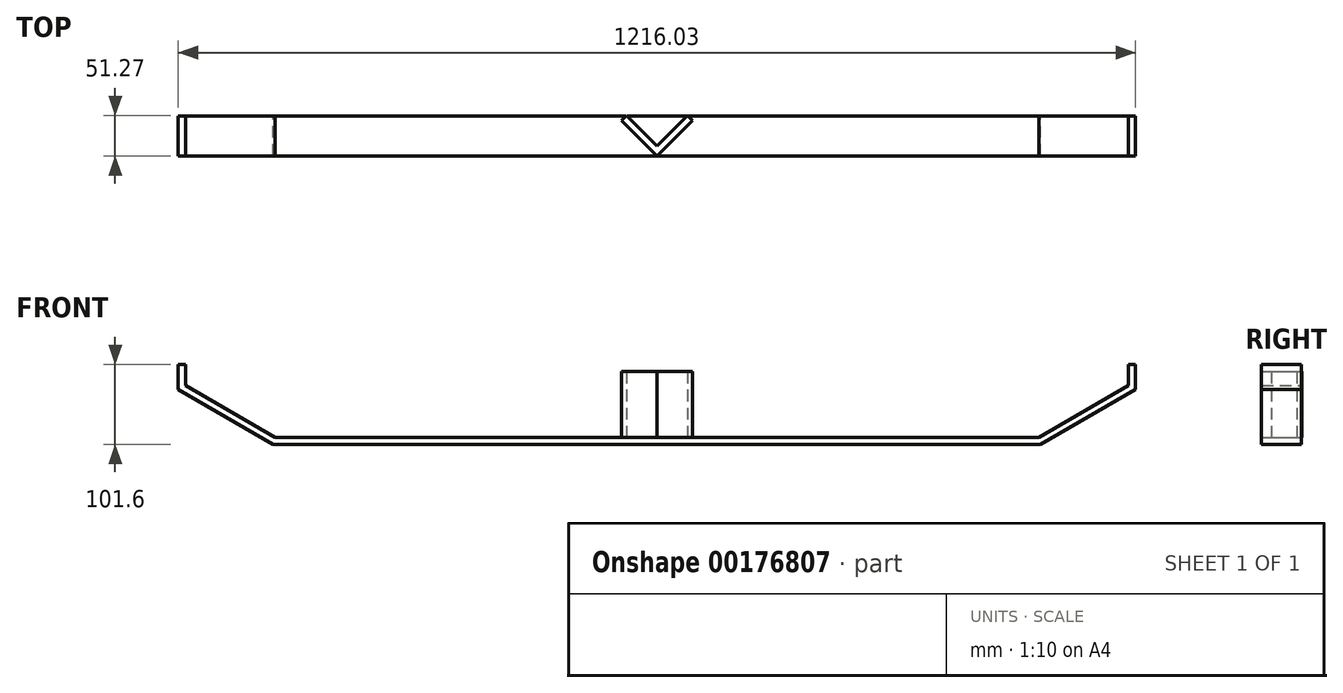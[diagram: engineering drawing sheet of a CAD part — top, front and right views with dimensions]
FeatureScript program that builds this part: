
annotation { "Feature Type Name" : "Feature", "Feature Type Description" : "" }
export const myFeature = defineFeature(function(context is Context, id is Id, definition is map)
    precondition{}
    {
        {
            var Q0;
            Q0=qCreatedBy(makeId("Front.planeOp"),FACE);
            var sketch = newSketch(context, id + "F0", { "sketchPlane" : qUnion([Q0])});
            skLineSegment(sketch, "E0", {"start": v(0, 0) * mm, "end": v(974.73, 0) * mm});
            skLineSegment(sketch, "E1.0", {"start": v(1095.38, 69.66) * mm, "end": v(1095.38, 101.6) * mm});
            skLineSegment(sketch, "E2", {"start": v(974.73, 0) * mm, "end": v(1095.38, 69.66) * mm});
            skLineSegment(sketch, "E3", {"start": v(487.36, 0) * mm, "end": v(487.36, 114.97) * mm});
            skLineSegment(sketch, "E4.MirrorCS", {"start": v(0, 0) * mm, "end": v(-120.65, 69.66) * mm});
            skLineSegment(sketch, "E5.MirrorCS", {"start": v(-120.65, 69.66) * mm, "end": v(-120.65, 101.6) * mm});
            skLineSegment(sketch, "E6.0", {"start": v(-111.65, 74.85) * mm, "end": v(-111.65, 101.6) * mm});
            skLineSegment(sketch, "E7.0", {"start": v(2.41, 9) * mm, "end": v(-111.65, 74.85) * mm});
            skLineSegment(sketch, "E8.0", {"start": v(2.41, 9) * mm, "end": v(972.31, 9) * mm});
            skLineSegment(sketch, "E9.0", {"start": v(972.31, 9) * mm, "end": v(1086.38, 74.85) * mm});
            skLineSegment(sketch, "E10.0", {"start": v(1086.38, 74.85) * mm, "end": v(1086.38, 101.6) * mm});
            skLineSegment(sketch, "E11.filletArc", {"start": v(1086.38, 74.85) * mm, "end": v(1086.38, 74.85) * mm});
            skLineSegment(sketch, "E12.filletArc", {"start": v(972.31, 9) * mm, "end": v(972.31, 9) * mm});
            skLineSegment(sketch, "E13.filletArc", {"start": v(2.41, 9) * mm, "end": v(2.41, 9) * mm});
            skLineSegment(sketch, "E14.filletArc", {"start": v(-111.65, 74.85) * mm, "end": v(-111.65, 74.85) * mm});
            skLineSegment(sketch, "E15", {"start": v(1095.38, 101.6) * mm, "end": v(1086.38, 101.6) * mm});
            skLineSegment(sketch, "E16.filletArc", {"start": v(1086.38, 101.6) * mm, "end": v(1086.38, 101.6) * mm});
            skLineSegment(sketch, "E17", {"start": v(-120.65, 101.6) * mm, "end": v(-111.65, 101.6) * mm});
            skLineSegment(sketch, "E18.filletArc", {"start": v(-111.65, 101.6) * mm, "end": v(-111.65, 101.6) * mm});
            skSolve(sketch);
        }
        {
            var Q0;
            Q0=qCreatedBy(makeId("Top.planeOp"),FACE);
            var sketch = newSketch(context, id + "F1", { "sketchPlane" : qUnion([Q0])});
            skLineSegment(sketch, "E19", {"start": v(497.53, 179.1) * mm, "end": v(542.43, 224) * mm});
            skLineSegment(sketch, "E20", {"start": v(497.53, 179.1) * mm, "end": v(452.63, 224) * mm});
            skLineSegment(sketch, "E21.0", {"start": v(497.53, 191.83) * mm, "end": v(536.07, 230.37) * mm});
            skLineSegment(sketch, "E22", {"start": v(542.43, 224) * mm, "end": v(536.07, 230.37) * mm});
            skLineSegment(sketch, "E23.0", {"start": v(497.53, 191.83) * mm, "end": v(459, 230.37) * mm});
            skLineSegment(sketch, "E24", {"start": v(452.63, 224) * mm, "end": v(459, 230.37) * mm});
            skSolve(sketch);
        }
        {
            var Q0;
            {var subQ0=sQuery(id+"F0.wireOp",EDGE,"E4.MirrorCS");Q0=makeQuery(id+"F0.imprint","IMPRINT",FACE,{"disambiguationData":[TD([[makeQuery(id+"F0.imprint","IMPRINT",EDGE,{"derivedFrom":subQ0}),-1.0]])]});}
            var Q1;
            Q1=makeQuery(id+"F0.imprint","IMPRINT",FACE,{"disambiguationData":[TD([[makeQuery(id+"F0.imprint","IMPRINT",EDGE,{"derivedFrom":sQuery(id+"F0.wireOp",EDGE,"E1.0")}),1.0]])]});
            extrude(context, id + "F2", {"entities" : qUnion([Q0, Q1]), "depth" : 50.8 * mm});
        }
        {
            var Q0;
            Q0=makeQuery(id+"F1.imprint","IMPRINT",FACE,{"disambiguationData":[TD([[makeQuery(id+"F1.imprint","IMPRINT",EDGE,{"derivedFrom":sQuery(id+"F1.wireOp",EDGE,"E19")}),1.0]])]});
            extrude(context, id + "F3", {"entities" : qUnion([Q0]), "depth" : 83.6 * mm});
        }
        {
            var Q0;
            Q0=makeQuery(id+"F2.opExtrude","CAP_EDGE",EDGE,{"disambiguationData":[OSD([sQuery(id+"F0.wireOp",EDGE,"E8.0")])],"isStart":false});
            cPoint(context, id + "F4", {"entities" : qUnion([Q0]), "parameter" : 0.5});
        }
        {
            var Q0;
            Q0=makeQuery(id+"F3.opExtrude","SWEPT_BODY",BODY,{"disambiguationData":[OSD([sQuery(id+"F1.wireOp",EDGE,"E19"),sQuery(id+"F1.wireOp",EDGE,"E20"),sQuery(id+"F1.wireOp",EDGE,"E21.0"),sQuery(id+"F1.wireOp",EDGE,"E22"),sQuery(id+"F1.wireOp",EDGE,"E23.0"),sQuery(id+"F1.wireOp",EDGE,"E24")])]});
            var Q1;
            Q1=makeQuery(id+"F3.opExtrude","CAP_VERTEX",VERTEX,{"disambiguationData":[OSD([sQuery(id+"F1.wireOp",EDGE,"E19"),sQuery(id+"F1.wireOp",EDGE,"E20")])],"isStart":true});
            var Q2;
            Q2 = qCreatedBy(id + "F4" ,VERTEX);
            transform(context, id + "F5", {"entities" : qUnion([Q0]), "transformType" : TransformType.TRANSLATION_ENTITY, "oppositeDirectionEntity" : false, "transformLine" : qUnion([Q1, Q2]), "makeCopy" : false});
        }
    });
